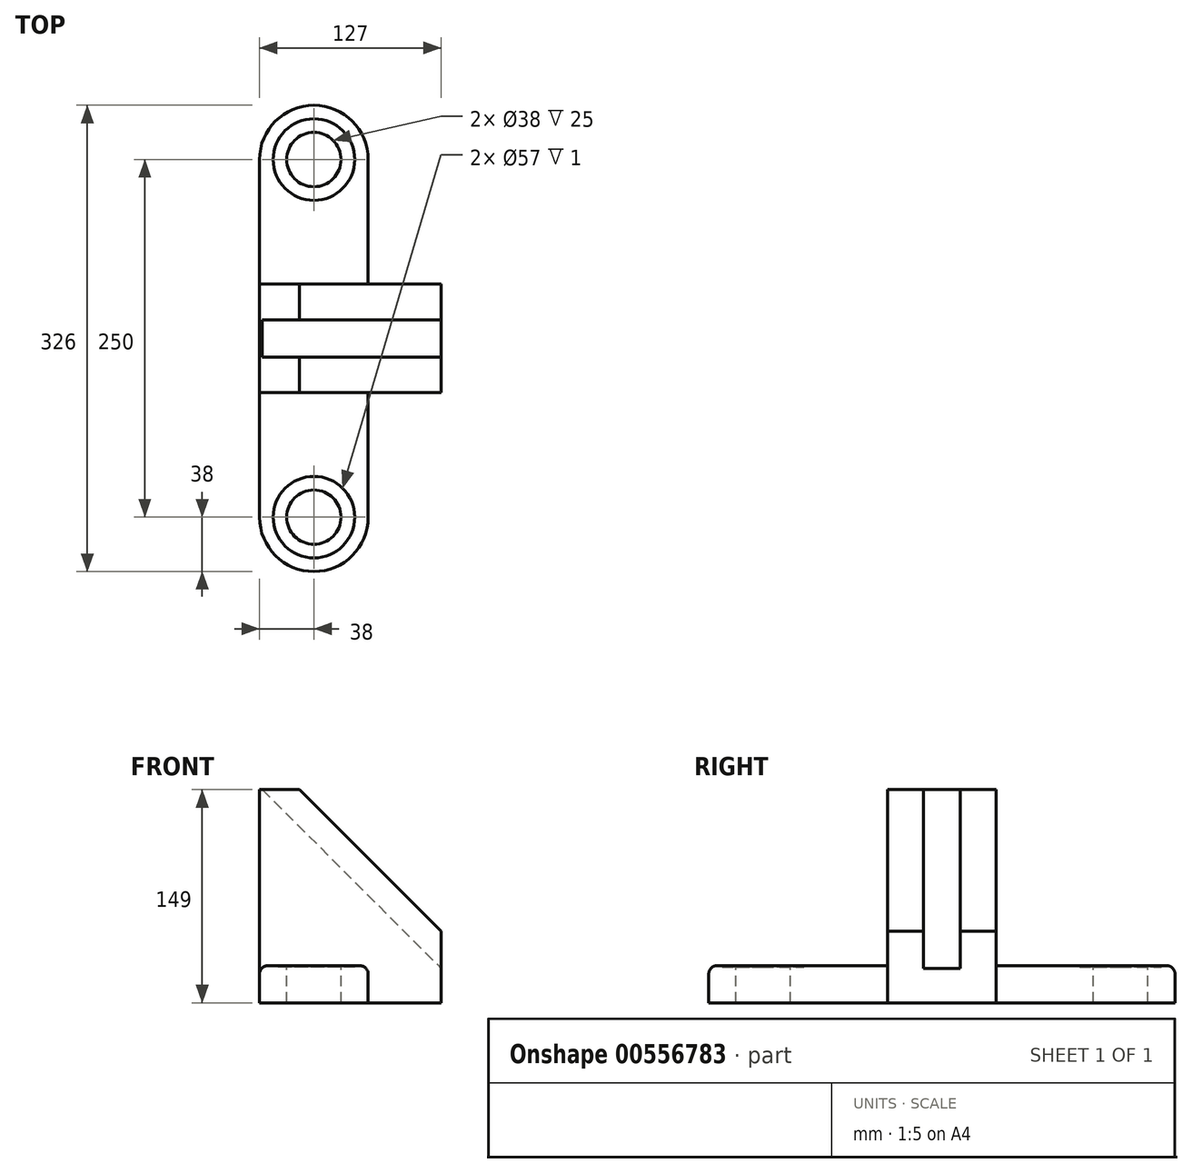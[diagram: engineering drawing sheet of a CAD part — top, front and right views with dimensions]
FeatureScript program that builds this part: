
annotation { "Feature Type Name" : "Feature", "Feature Type Description" : "" }
export const myFeature = defineFeature(function(context is Context, id is Id, definition is map)
    precondition{}
    {
        {
            var Q0;
            Q0=qCreatedBy(makeId("Front.planeOp"),FACE);
            var sketch = newSketch(context, id + "F0", { "sketchPlane" : qUnion([Q0])});
            skLineSegment(sketch, "E0", {"start": v(0, 0) * mm, "end": v(127, 0) * mm});
            skLineSegment(sketch, "E1", {"start": v(127, 0) * mm, "end": v(127, 50) * mm});
            skLineSegment(sketch, "E2", {"start": v(0, 0) * mm, "end": v(0, 149) * mm});
            skLineSegment(sketch, "E3", {"start": v(127, 50) * mm, "end": v(18.66, 158.34) * mm});
            skLineSegment(sketch, "E4", {"start": v(0, 149) * mm, "end": v(28, 149) * mm});
            skSolve(sketch);
        }
        {
            var Q0;
            Q0=qSketchRegion(id+"F0",true);
            extrude(context, id + "F1", {"entities" : qUnion([Q0]), "endBound" : BoundingType.SYMMETRIC, "depth" : 76 * mm, "offsetDistance" : 25 * mm});
        }
        {
            var Q0;
            Q0=makeQuery(id+"F1.opExtrude","SWEPT_FACE",FACE,{"disambiguationData":[OSD([sQuery(id+"F0.wireOp",EDGE,"E0")])]});
            var sketch = newSketch(context, id + "F2", { "sketchPlane" : qUnion([Q0])});
            skLineSegment(sketch, "E5", {"start": v(38, -125) * mm, "end": v(38, 125) * mm, "construction": true});
            skLineSegment(sketch, "E6", {"start": v(0, 0) * mm, "end": v(133.16, 0) * mm, "construction": true});
            skPoint(sketch, "E6.endSnap0", {"position": v(127, 0) * mm});
            skArc(sketch, "E7.0.startCap", {"start": v(76, -125) * mm, "mid": v(38, -163) * mm, "end": v(0, -125) * mm});
            skArc(sketch, "E7.0.endCap", {"start": v(0, 125) * mm, "mid": v(38, 163) * mm, "end": v(76, 125) * mm});
            skLineSegment(sketch, "E7.0.left", {"start": v(0, -125) * mm, "end": v(0, 125) * mm});
            skLineSegment(sketch, "E7.0.right", {"start": v(76, -125) * mm, "end": v(76, 125) * mm});
            skSolve(sketch);
        }
        {
            var Q0;
            Q0=qCreatedBy(makeId("Front.planeOp"),FACE);
            var sketch = newSketch(context, id + "F3", { "sketchPlane" : qUnion([Q0])});
            skLineSegment(sketch, "E8", {"start": v(28, 149) * mm, "end": v(2, 149) * mm});
            skLineSegment(sketch, "E9", {"start": v(28, 149) * mm, "end": v(127, 50) * mm});
            skLineSegment(sketch, "E10", {"start": v(2, 149) * mm, "end": v(127, 24) * mm});
            skLineSegment(sketch, "E11", {"start": v(127, 50) * mm, "end": v(127, 24) * mm});
            skSolve(sketch);
        }
        {
            var Q0;
            Q0=qSketchRegion(id+"F3",true);
            extrude(context, id + "F4", {"entities" : qUnion([Q0]), "operationType" : NewBodyOperationType.REMOVE, "endBound" : BoundingType.SYMMETRIC, "oppositeDirection" : true, "depth" : 26 * mm, "offsetDistance" : 25 * mm});
        }
        {
            var Q0;
            Q0=qSketchRegion(id+"F2",true);
            extrude(context, id + "F5", {"entities" : qUnion([Q0]), "operationType" : NewBodyOperationType.ADD, "oppositeDirection" : true, "depth" : 26 * mm, "offsetDistance" : 25 * mm});
        }
        {
            var Q0;
            {var subQ0=sQuery(id+"F2.wireOp",EDGE,"E7.0.left");var subQ1=sQuery(id+"F2.wireOp",EDGE,"E7.0.endCap");var subQ3=sQuery(id+"F2.wireOp",EDGE,"E7.0.right");Q0=makeQuery(id+"F5.boolean.opBoolean","SPLIT",FACE,{"disambiguationData":[TD([makeQuery(id+"F5.opExtrude","SWEPT_FACE",FACE,{"disambiguationData":[OSD([subQ1])]})])],"derivedFrom":makeQuery(id+"F5.opExtrude","CAP_FACE",FACE,{"disambiguationData":[OSD([sQuery(id+"F2.wireOp",EDGE,"E7.0.startCap"),subQ1,subQ0,subQ3])],"isStart":false})});}
            var sketch = newSketch(context, id + "F6", { "sketchPlane" : qUnion([Q0])});
            skLineSegment(sketch, "E12", {"start": v(0, -125) * mm, "end": v(76, -125) * mm, "construction": true});
            skLineSegment(sketch, "E13", {"start": v(38, -163) * mm, "end": v(38, -102.67) * mm, "construction": true});
            skCircle(sketch, "E14", {"center": v(38, -125) * mm, "radius": 19 * mm});
            skSolve(sketch);
        }
        {
            var Q0;
            Q0=qSketchRegion(id+"F6",true);
            extrude(context, id + "F7", {"entities" : qUnion([Q0]), "operationType" : NewBodyOperationType.REMOVE, "endBound" : BoundingType.THROUGH_ALL, "oppositeDirection" : true, "depth" : 25 * mm, "offsetDistance" : 25 * mm});
        }
        {
            var Q0;
            {var subQ0=sQuery(id+"F2.wireOp",EDGE,"E7.0.left");var subQ1=sQuery(id+"F2.wireOp",EDGE,"E7.0.endCap");var subQ3=sQuery(id+"F2.wireOp",EDGE,"E7.0.right");Q0=makeQuery(id+"F5.boolean.opBoolean","SPLIT",FACE,{"disambiguationData":[TD([makeQuery(id+"F5.opExtrude","SWEPT_FACE",FACE,{"disambiguationData":[OSD([subQ1])]})])],"derivedFrom":makeQuery(id+"F5.opExtrude","CAP_FACE",FACE,{"disambiguationData":[OSD([sQuery(id+"F2.wireOp",EDGE,"E7.0.startCap"),subQ1,subQ0,subQ3])],"isStart":false})});}
            var sketch = newSketch(context, id + "F8", { "sketchPlane" : qUnion([Q0])});
            skLineSegment(sketch, "E15", {"start": v(0, -125) * mm, "end": v(76, -125) * mm, "construction": true});
            skLineSegment(sketch, "E16", {"start": v(38, -163) * mm, "end": v(38, -98.55) * mm, "construction": true});
            skCircle(sketch, "E17", {"center": v(38, -125) * mm, "radius": 28.5 * mm});
            skSolve(sketch);
        }
        {
            var Q0;
            Q0=qSketchRegion(id+"F8",true);
            extrude(context, id + "F9", {"entities" : qUnion([Q0]), "operationType" : NewBodyOperationType.REMOVE, "oppositeDirection" : true, "depth" : 1 * mm, "offsetDistance" : 25 * mm});
        }
        {
            var Q0;
            {var subQ0=sQuery(id+"F2.wireOp",EDGE,"E7.0.startCap");var subQ2=sQuery(id+"F2.wireOp",EDGE,"E7.0.left");var subQ3=sQuery(id+"F2.wireOp",EDGE,"E7.0.right");Q0=makeQuery(id+"F5.boolean.opBoolean","SPLIT",FACE,{"disambiguationData":[TD([makeQuery(id+"F5.opExtrude","SWEPT_FACE",FACE,{"disambiguationData":[OSD([subQ0])]})])],"derivedFrom":makeQuery(id+"F5.opExtrude","CAP_FACE",FACE,{"disambiguationData":[OSD([subQ0,sQuery(id+"F2.wireOp",EDGE,"E7.0.endCap"),subQ2,subQ3])],"isStart":false})});}
            var sketch = newSketch(context, id + "F10", { "sketchPlane" : qUnion([Q0])});
            skLineSegment(sketch, "E18", {"start": v(0, 125) * mm, "end": v(76, 125) * mm, "construction": true});
            skLineSegment(sketch, "E19", {"start": v(38, 163) * mm, "end": v(38, 68.58) * mm, "construction": true});
            skPoint(sketch, "E19.endSnap0", {"position": v(38, 163) * mm});
            skCircle(sketch, "E20", {"center": v(38, 125) * mm, "radius": 19 * mm});
            skSolve(sketch);
        }
        {
            var Q0;
            Q0=qSketchRegion(id+"F10",true);
            extrude(context, id + "F11", {"entities" : qUnion([Q0]), "operationType" : NewBodyOperationType.REMOVE, "endBound" : BoundingType.THROUGH_ALL, "oppositeDirection" : true, "depth" : 25 * mm, "offsetDistance" : 25 * mm});
        }
        {
            var Q0;
            {var subQ0=sQuery(id+"F2.wireOp",EDGE,"E7.0.startCap");var subQ2=sQuery(id+"F2.wireOp",EDGE,"E7.0.left");var subQ3=sQuery(id+"F2.wireOp",EDGE,"E7.0.right");Q0=makeQuery(id+"F5.boolean.opBoolean","SPLIT",FACE,{"disambiguationData":[TD([makeQuery(id+"F5.opExtrude","SWEPT_FACE",FACE,{"disambiguationData":[OSD([subQ0])]})])],"derivedFrom":makeQuery(id+"F5.opExtrude","CAP_FACE",FACE,{"disambiguationData":[OSD([subQ0,sQuery(id+"F2.wireOp",EDGE,"E7.0.endCap"),subQ2,subQ3])],"isStart":false})});}
            var sketch = newSketch(context, id + "F12", { "sketchPlane" : qUnion([Q0])});
            skLineSegment(sketch, "E21", {"start": v(0, 125) * mm, "end": v(76, 125) * mm, "construction": true});
            skLineSegment(sketch, "E22", {"start": v(38, 163) * mm, "end": v(38, 90.3) * mm, "construction": true});
            skPoint(sketch, "E22.endSnap0", {"position": v(38, 163) * mm});
            skCircle(sketch, "E23", {"center": v(38, 125) * mm, "radius": 28.5 * mm});
            skSolve(sketch);
        }
        {
            var Q0;
            Q0=qSketchRegion(id+"F12",true);
            extrude(context, id + "F13", {"entities" : qUnion([Q0]), "operationType" : NewBodyOperationType.REMOVE, "oppositeDirection" : true, "depth" : 1 * mm, "offsetDistance" : 25 * mm});
        }
        {
            var Q0;
            {var subQ0=sQuery(id+"F2.wireOp",EDGE,"E7.0.right");var subQ1=sQuery(id+"F2.wireOp",EDGE,"E7.0.endCap");Q0=makeQuery(id+"F5.boolean.opBoolean","SPLIT",EDGE,{"disambiguationData":[TD([makeQuery(id+"F5.opExtrude","SWEPT_FACE",FACE,{"disambiguationData":[OSD([subQ1])]})])],"derivedFrom":makeQuery(id+"F5.opExtrude","CAP_EDGE",EDGE,{"disambiguationData":[OSD([subQ0])],"isStart":false})});}
            var Q1;
            {var subQ0=sQuery(id+"F2.wireOp",EDGE,"E7.0.endCap");var subQ1=sQuery(id+"F2.wireOp",EDGE,"E7.0.left");Q1=makeQuery(id+"F5.boolean.opBoolean","SPLIT",EDGE,{"disambiguationData":[TD([makeQuery(id+"F5.opExtrude","SWEPT_FACE",FACE,{"disambiguationData":[OSD([subQ0])]})])],"derivedFrom":makeQuery(id+"F5.opExtrude","CAP_EDGE",EDGE,{"disambiguationData":[OSD([subQ1])],"isStart":false})});}
            var Q2;
            Q2=makeQuery(id+"F5.opExtrude","CAP_EDGE",EDGE,{"disambiguationData":[OSD([sQuery(id+"F2.wireOp",EDGE,"E7.0.endCap")])],"isStart":false});
            var Q3;
            {var subQ0=sQuery(id+"F2.wireOp",EDGE,"E7.0.startCap");var subQ1=sQuery(id+"F2.wireOp",EDGE,"E7.0.right");Q3=makeQuery(id+"F5.boolean.opBoolean","SPLIT",EDGE,{"disambiguationData":[TD([makeQuery(id+"F5.opExtrude","SWEPT_FACE",FACE,{"disambiguationData":[OSD([subQ0])]})])],"derivedFrom":makeQuery(id+"F5.opExtrude","CAP_EDGE",EDGE,{"disambiguationData":[OSD([subQ1])],"isStart":false})});}
            var Q4;
            Q4=makeQuery(id+"F5.opExtrude","CAP_EDGE",EDGE,{"disambiguationData":[OSD([sQuery(id+"F2.wireOp",EDGE,"E7.0.startCap")])],"isStart":false});
            var Q5;
            {var subQ0=sQuery(id+"F2.wireOp",EDGE,"E7.0.startCap");var subQ1=sQuery(id+"F2.wireOp",EDGE,"E7.0.left");Q5=makeQuery(id+"F5.boolean.opBoolean","SPLIT",EDGE,{"disambiguationData":[TD([makeQuery(id+"F5.opExtrude","SWEPT_FACE",FACE,{"disambiguationData":[OSD([subQ0])]})])],"derivedFrom":makeQuery(id+"F5.opExtrude","CAP_EDGE",EDGE,{"disambiguationData":[OSD([subQ1])],"isStart":false})});}
            fillet(context, id + "F14", {"entities" : qUnion([Q0, Q1, Q2, Q3, Q4, Q5]), "radius" : 6 * mm, "tangentPropagation" : true, "allowEdgeOverflow" : false});
        }
    });
